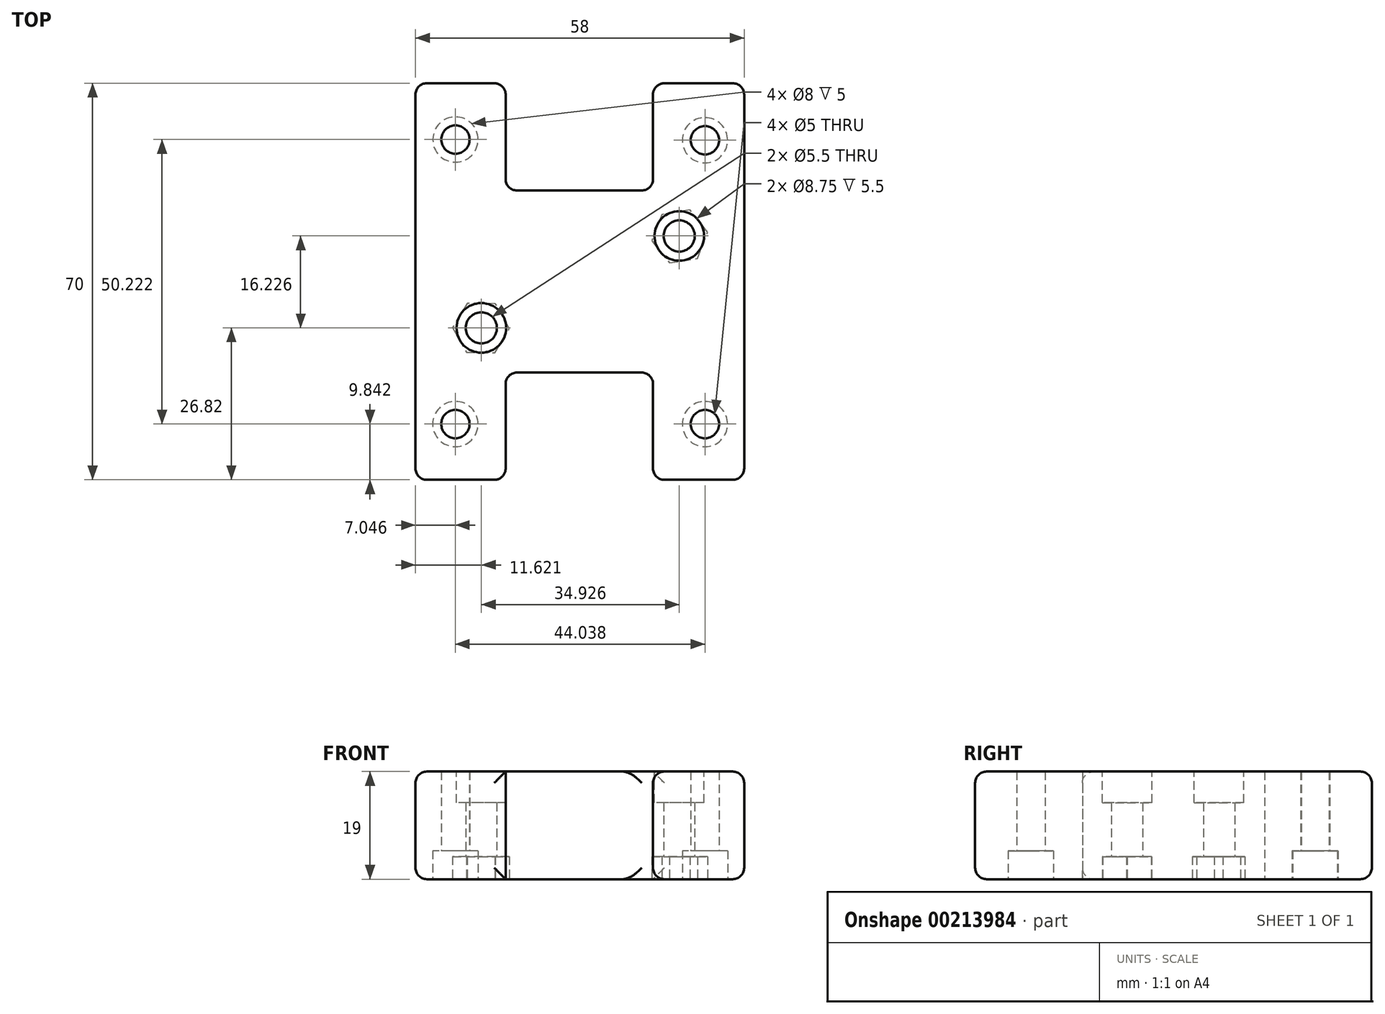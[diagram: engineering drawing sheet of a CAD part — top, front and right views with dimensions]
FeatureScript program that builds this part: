
annotation { "Feature Type Name" : "Feature", "Feature Type Description" : "" }
export const myFeature = defineFeature(function(context is Context, id is Id, definition is map)
    precondition{}
    {
        {
            var Q0;
            Q0=qCreatedBy(makeId("Top.planeOp"),FACE);
            var sketch = newSketch(context, id + "F0", { "sketchPlane" : qUnion([Q0])});
            skLineSegment(sketch, "E0.bottom", {"start": v(-29, 35) * mm, "end": v(29, 35) * mm});
            skLineSegment(sketch, "E0.top", {"start": v(-29, -35) * mm, "end": v(29, -35) * mm});
            skLineSegment(sketch, "E0.left", {"start": v(-29, 35) * mm, "end": v(-29, -35) * mm});
            skLineSegment(sketch, "E0.right", {"start": v(29, 35) * mm, "end": v(29, -35) * mm});
            skPoint(sketch, "E0.middle", {"position": v(0, 0) * mm});
            skSolve(sketch);
        }
        {
            var Q0;
            Q0=qCreatedBy(makeId("Top.planeOp"),FACE);
            var sketch = newSketch(context, id + "F1", { "sketchPlane" : qUnion([Q0])});
            skLineSegment(sketch, "E1", {"start": v(-28.94, -35.1) * mm, "end": v(-21.94, -35.1) * mm});
            skLineSegment(sketch, "E2", {"start": v(-28.94, -35.1) * mm, "end": v(-28.94, -25.1) * mm});
            skLineSegment(sketch, "E3", {"start": v(-28.94, -25.1) * mm, "end": v(29.13, -25.1) * mm});
            skLineSegment(sketch, "E4", {"start": v(-21.94, -35.1) * mm, "end": v(-21.94, 34.92) * mm});
            skLineSegment(sketch, "E5", {"start": v(29.13, -25.1) * mm, "end": v(29.13, -35.1) * mm});
            skLineSegment(sketch, "E6", {"start": v(29.13, -35.1) * mm, "end": v(22.13, -35.1) * mm});
            skLineSegment(sketch, "E7", {"start": v(22.13, -35.1) * mm, "end": v(22.13, 34.86) * mm});
            skLineSegment(sketch, "E8", {"start": v(22.13, 34.86) * mm, "end": v(29.13, 34.86) * mm});
            skLineSegment(sketch, "E9", {"start": v(29.13, 34.86) * mm, "end": v(29.13, 24.86) * mm});
            skLineSegment(sketch, "E10", {"start": v(29.13, 24.86) * mm, "end": v(-28.94, 24.86) * mm});
            skLineSegment(sketch, "E11", {"start": v(-28.94, 24.86) * mm, "end": v(-28.94, 34.86) * mm});
            skLineSegment(sketch, "E12", {"start": v(-28.94, 34.86) * mm, "end": v(-21.94, 34.92) * mm});
            skLineSegment(sketch, "E13", {"start": v(29.13, 34.86) * mm, "end": v(29.13, 7.96) * mm});
            skLineSegment(sketch, "E14", {"start": v(29.13, 7.96) * mm, "end": v(17.63, 7.96) * mm});
            skLineSegment(sketch, "E15", {"start": v(-28.94, -35.1) * mm, "end": v(-28.94, -8.2) * mm});
            skLineSegment(sketch, "E16", {"start": v(-28.94, -8.2) * mm, "end": v(-17.44, -8.2) * mm});
            skLineSegment(sketch, "E17", {"start": v(-28.94, -25.1) * mm, "end": v(-12.94, -25.1) * mm});
            skLineSegment(sketch, "E18", {"start": v(-12.94, -25.1) * mm, "end": v(-12.94, -16.1) * mm});
            skLineSegment(sketch, "E19", {"start": v(-12.94, -16.1) * mm, "end": v(-12.94, -35.1) * mm});
            skLineSegment(sketch, "E20.MirrorCS", {"start": v(12.94, -16.1) * mm, "end": v(12.94, -35.1) * mm});
            skLineSegment(sketch, "E21.MirrorCS", {"start": v(-12.94, 16.1) * mm, "end": v(-12.94, 35.1) * mm});
            skLineSegment(sketch, "E22.MirrorCS", {"start": v(12.94, 16.1) * mm, "end": v(12.94, 35.1) * mm});
            skSolve(sketch);
        }
        {
            var Q0;
            Q0=qCreatedBy(makeId("Top.planeOp"),FACE);
            var sketch = newSketch(context, id + "F2", { "sketchPlane" : qUnion([Q0])});
            skCircle(sketch, "E23", {"center": v(-21.94, 25.06) * mm, "radius": 4 * mm});
            skCircle(sketch, "E24", {"center": v(-21.95, -25.16) * mm, "radius": 4 * mm});
            skCircle(sketch, "E25", {"center": v(22.08, -25.16) * mm, "radius": 4 * mm});
            skCircle(sketch, "E26", {"center": v(22.08, 24.94) * mm, "radius": 4 * mm});
            skSolve(sketch);
        }
        {
            var Q0;
            Q0=qCreatedBy(makeId("Top.planeOp"),FACE);
            var sketch = newSketch(context, id + "F3", { "sketchPlane" : qUnion([Q0])});
            skCircle(sketch, "E27", {"center": v(-21.94, 25.06) * mm, "radius": 2.5 * mm});
            skCircle(sketch, "E28", {"center": v(22.08, 24.94) * mm, "radius": 2.5 * mm});
            skCircle(sketch, "E29", {"center": v(-21.95, -25.16) * mm, "radius": 2.5 * mm});
            skCircle(sketch, "E30", {"center": v(22.08, -25.16) * mm, "radius": 2.5 * mm});
            skSolve(sketch);
        }
        {
            var Q0;
            Q0=makeQuery(id+"F0.imprint","IMPRINT",FACE,{"disambiguationData":[TD([[makeQuery(id+"F0.imprint","IMPRINT",EDGE,{"derivedFrom":sQuery(id+"F0.wireOp",EDGE,"E0.bottom")}),-1.0]])]});
            extrude(context, id + "F4", {"entities" : qUnion([Q0]), "offsetDistance" : 25 * mm, "depth" : 19 * mm});
        }
        {
            var Q0;
            Q0=makeQuery(id+"F3.imprint","IMPRINT",FACE,{"disambiguationData":[TD([[makeQuery(id+"F3.imprint","IMPRINT",EDGE,{"derivedFrom":sQuery(id+"F3.wireOp",EDGE,"E27")}),1.0]])]});
            extrude(context, id + "F5", {"entities" : qUnion([Q0]), "operationType" : NewBodyOperationType.REMOVE, "depth" : 14 * mm});
        }
        {
            var Q0;
            Q0=makeQuery(id+"F2.imprint","IMPRINT",FACE,{"disambiguationData":[TD([[makeQuery(id+"F2.imprint","IMPRINT",EDGE,{"derivedFrom":sQuery(id+"F2.wireOp",EDGE,"E23")}),1.0]])]});
            extrude(context, id + "F6", {"entities" : qUnion([Q0]), "operationType" : NewBodyOperationType.REMOVE, "offsetDistance" : 25 * mm, "depth" : 5 * mm});
        }
        {
            var Q0;
            Q0 = qSketchRegion(id + "F3", true);
            extrude(context, id + "F7", {"entities" : qUnion([Q0]), "operationType" : NewBodyOperationType.REMOVE, "offsetDistance" : 25 * mm, "depth" : 19 * mm});
        }
        {
            var Q0;
            Q0 = qSketchRegion(id + "F2", true);
            extrude(context, id + "F8", {"entities" : qUnion([Q0]), "operationType" : NewBodyOperationType.REMOVE, "depth" : 5 * mm});
        }
        {
            var Q0;
            Q0=qCreatedBy(makeId("Top.planeOp"),FACE);
            var sketch = newSketch(context, id + "F9", { "sketchPlane" : qUnion([Q0])});
            skCircle(sketch, "E31", {"center": v(17.55, 8.05) * mm, "radius": 2.75 * mm});
            skCircle(sketch, "E32", {"center": v(-17.38, -8.18) * mm, "radius": 2.75 * mm});
            skSolve(sketch);
        }
        {
            var Q0;
            Q0 = qSketchRegion(id + "F9", true);
            extrude(context, id + "F10", {"entities" : qUnion([Q0]), "operationType" : NewBodyOperationType.REMOVE, "offsetDistance" : 25 * mm, "depth" : 19 * mm});
        }
        {
            var Q0;
            Q0=makeQuery(id+"F4.opExtrude","CAP_FACE",FACE,{"disambiguationData":[OSD([sQuery(id+"F0.wireOp",EDGE,"E0.bottom"),sQuery(id+"F0.wireOp",EDGE,"E0.top"),sQuery(id+"F0.wireOp",EDGE,"E0.left"),sQuery(id+"F0.wireOp",EDGE,"E0.right")])],"isStart":true});
            var sketch = newSketch(context, id + "F11", { "sketchPlane" : qUnion([Q0])});
            skCircle(sketch, "E33.cCircle", {"center": v(-17.44, 8.2) * mm, "radius": 5 * mm, "construction": true});
            skLineSegment(sketch, "E33.0", {"start": v(-20, 12.5) * mm, "end": v(-15, 12.57) * mm});
            skLineSegment(sketch, "E33.1", {"start": v(-15, 12.57) * mm, "end": v(-12.44, 8.28) * mm});
            skLineSegment(sketch, "E33.2", {"start": v(-12.44, 8.28) * mm, "end": v(-14.88, 3.91) * mm});
            skLineSegment(sketch, "E33.3", {"start": v(-14.88, 3.91) * mm, "end": v(-19.88, 3.84) * mm});
            skLineSegment(sketch, "E33.4", {"start": v(-19.88, 3.84) * mm, "end": v(-22.44, 8.14) * mm});
            skLineSegment(sketch, "E33.5", {"start": v(-22.44, 8.14) * mm, "end": v(-20, 12.5) * mm});
            skCircle(sketch, "E34.cCircle", {"center": v(17.63, -7.96) * mm, "radius": 5 * mm, "construction": true});
            skLineSegment(sketch, "E34.0", {"start": v(22.57, -8.74) * mm, "end": v(19.42, -12.63) * mm});
            skLineSegment(sketch, "E34.1", {"start": v(19.42, -12.63) * mm, "end": v(14.49, -11.85) * mm});
            skLineSegment(sketch, "E34.2", {"start": v(14.49, -11.85) * mm, "end": v(12.69, -7.19) * mm});
            skLineSegment(sketch, "E34.3", {"start": v(12.69, -7.19) * mm, "end": v(15.83, -3.3) * mm});
            skLineSegment(sketch, "E34.4", {"start": v(15.83, -3.3) * mm, "end": v(20.77, -4.07) * mm});
            skLineSegment(sketch, "E34.5", {"start": v(20.77, -4.07) * mm, "end": v(22.57, -8.74) * mm});
            skSolve(sketch);
        }
        {
            var Q0;
            Q0 = qSketchRegion(id + "F11", true);
            extrude(context, id + "F12", {"entities" : qUnion([Q0]), "operationType" : NewBodyOperationType.REMOVE, "oppositeDirection" : true, "offsetDistance" : 25 * mm, "depth" : 4 * mm});
        }
        {
            var Q0;
            Q0=qCreatedBy(makeId("Top.planeOp"),FACE);
            var sketch = newSketch(context, id + "F13", { "sketchPlane" : qUnion([Q0])});
            skLineSegment(sketch, "E35.bottom", {"start": v(-13.1, 16.07) * mm, "end": v(12.9, 16.07) * mm});
            skLineSegment(sketch, "E35.top", {"start": v(-13.1, 35.07) * mm, "end": v(12.9, 35.07) * mm});
            skLineSegment(sketch, "E35.left", {"start": v(-13.1, 16.07) * mm, "end": v(-13.1, 35.07) * mm});
            skLineSegment(sketch, "E35.right", {"start": v(12.9, 16.07) * mm, "end": v(12.9, 35.07) * mm});
            skLineSegment(sketch, "E36.MirrorCS", {"start": v(-13.1, -16.07) * mm, "end": v(12.9, -16.07) * mm});
            skLineSegment(sketch, "E37.MirrorCS", {"start": v(-13.1, -16.07) * mm, "end": v(-13.1, -35.07) * mm});
            skLineSegment(sketch, "E38.MirrorCS", {"start": v(12.9, -16.07) * mm, "end": v(12.9, -35.07) * mm});
            skLineSegment(sketch, "E39.MirrorCS", {"start": v(-13.1, -35.07) * mm, "end": v(12.9, -35.07) * mm});
            skSolve(sketch);
        }
        {
            var Q0;
            Q0 = qSketchRegion(id + "F13", true);
            extrude(context, id + "F14", {"entities" : qUnion([Q0]), "operationType" : NewBodyOperationType.REMOVE, "offsetDistance" : 25 * mm, "depth" : 19 * mm});
        }
        {
            var Q0;
            Q0=makeQuery(id+"F14.boolean.opBoolean","COPY",EDGE,{"derivedFrom":makeQuery(id+"F14.opExtrude","CAP_EDGE",EDGE,{"disambiguationData":[OSD([sQuery(id+"F13.wireOp",EDGE,"E35.left")])],"isStart":true})});
            var Q1;
            Q1=makeQuery(id+"F14.boolean.opBoolean","COPY",EDGE,{"derivedFrom":makeQuery(id+"F14.opExtrude","CAP_EDGE",EDGE,{"disambiguationData":[OSD([sQuery(id+"F13.wireOp",EDGE,"E35.bottom")])],"isStart":true})});
            var Q2;
            Q2=makeQuery(id+"F14.boolean.opBoolean","COPY",EDGE,{"derivedFrom":makeQuery(id+"F14.opExtrude","CAP_EDGE",EDGE,{"disambiguationData":[OSD([sQuery(id+"F13.wireOp",EDGE,"E35.right")])],"isStart":true})});
            var Q3;
            {var subQ0=sQuery(id+"F0.wireOp",EDGE,"E0.bottom");var subQ1=sQuery(id+"F0.wireOp",EDGE,"E0.left");Q3=makeQuery(id+"F14.boolean.opBoolean","SPLIT",EDGE,{"disambiguationData":[TD([makeQuery(id+"F4.opExtrude","SWEPT_FACE",FACE,{"disambiguationData":[OSD([subQ1])]})])],"derivedFrom":makeQuery(id+"F4.opExtrude","CAP_EDGE",EDGE,{"disambiguationData":[OSD([subQ0])],"isStart":true})});}
            var Q4;
            Q4=makeQuery(id+"F4.opExtrude","CAP_EDGE",EDGE,{"disambiguationData":[OSD([sQuery(id+"F0.wireOp",EDGE,"E0.left")])],"isStart":true});
            var Q5;
            {var subQ0=sQuery(id+"F0.wireOp",EDGE,"E0.left");var subQ1=sQuery(id+"F0.wireOp",EDGE,"E0.top");Q5=makeQuery(id+"F14.boolean.opBoolean","SPLIT",EDGE,{"disambiguationData":[TD([makeQuery(id+"F4.opExtrude","SWEPT_FACE",FACE,{"disambiguationData":[OSD([subQ0])]})])],"derivedFrom":makeQuery(id+"F4.opExtrude","CAP_EDGE",EDGE,{"disambiguationData":[OSD([subQ1])],"isStart":true})});}
            var Q6;
            Q6=makeQuery(id+"F14.boolean.opBoolean","COPY",EDGE,{"derivedFrom":makeQuery(id+"F14.opExtrude","CAP_EDGE",EDGE,{"disambiguationData":[OSD([sQuery(id+"F13.wireOp",EDGE,"E37.MirrorCS")])],"isStart":true})});
            var Q7;
            Q7=makeQuery(id+"F14.boolean.opBoolean","COPY",EDGE,{"derivedFrom":makeQuery(id+"F14.opExtrude","CAP_EDGE",EDGE,{"disambiguationData":[OSD([sQuery(id+"F13.wireOp",EDGE,"E36.MirrorCS")])],"isStart":true})});
            var Q8;
            Q8=makeQuery(id+"F14.boolean.opBoolean","COPY",EDGE,{"derivedFrom":makeQuery(id+"F14.opExtrude","CAP_EDGE",EDGE,{"disambiguationData":[OSD([sQuery(id+"F13.wireOp",EDGE,"E38.MirrorCS")])],"isStart":true})});
            var Q9;
            {var subQ0=sQuery(id+"F0.wireOp",EDGE,"E0.right");var subQ1=sQuery(id+"F0.wireOp",EDGE,"E0.top");Q9=makeQuery(id+"F14.boolean.opBoolean","SPLIT",EDGE,{"disambiguationData":[TD([makeQuery(id+"F4.opExtrude","SWEPT_FACE",FACE,{"disambiguationData":[OSD([subQ0])]})])],"derivedFrom":makeQuery(id+"F4.opExtrude","CAP_EDGE",EDGE,{"disambiguationData":[OSD([subQ1])],"isStart":true})});}
            var Q10;
            Q10=makeQuery(id+"F4.opExtrude","CAP_EDGE",EDGE,{"disambiguationData":[OSD([sQuery(id+"F0.wireOp",EDGE,"E0.right")])],"isStart":true});
            var Q11;
            {var subQ0=sQuery(id+"F0.wireOp",EDGE,"E0.bottom");var subQ1=sQuery(id+"F0.wireOp",EDGE,"E0.right");Q11=makeQuery(id+"F14.boolean.opBoolean","SPLIT",EDGE,{"disambiguationData":[TD([makeQuery(id+"F4.opExtrude","SWEPT_FACE",FACE,{"disambiguationData":[OSD([subQ1])]})])],"derivedFrom":makeQuery(id+"F4.opExtrude","CAP_EDGE",EDGE,{"disambiguationData":[OSD([subQ0])],"isStart":true})});}
            var Q12;
            Q12=makeQuery(id+"F14.boolean.opBoolean","INTERSECT",EDGE,{"derivedFrom":[makeQuery(id+"F4.opExtrude","SWEPT_FACE",FACE,{"disambiguationData":[OSD([sQuery(id+"F0.wireOp",EDGE,"E0.bottom")])]}),makeQuery(id+"F14.opExtrude","SWEPT_FACE",FACE,{"disambiguationData":[OSD([sQuery(id+"F13.wireOp",EDGE,"E35.left")])]})]});
            var Q13;
            Q13=makeQuery(id+"F14.boolean.opBoolean","COPY",EDGE,{"derivedFrom":makeQuery(id+"F14.opExtrude","SWEPT_EDGE",EDGE,{"disambiguationData":[OSD([sQuery(id+"F13.wireOp",EDGE,"E35.bottom"),sQuery(id+"F13.wireOp",EDGE,"E35.left")])]})});
            var Q14;
            Q14=makeQuery(id+"F14.boolean.opBoolean","INTERSECT",EDGE,{"derivedFrom":[makeQuery(id+"F4.opExtrude","SWEPT_FACE",FACE,{"disambiguationData":[OSD([sQuery(id+"F0.wireOp",EDGE,"E0.bottom")])]}),makeQuery(id+"F14.opExtrude","SWEPT_FACE",FACE,{"disambiguationData":[OSD([sQuery(id+"F13.wireOp",EDGE,"E35.right")])]})]});
            var Q15;
            Q15=makeQuery(id+"F4.opExtrude","SWEPT_EDGE",EDGE,{"disambiguationData":[OSD([sQuery(id+"F0.wireOp",EDGE,"E0.bottom"),sQuery(id+"F0.wireOp",EDGE,"E0.right")])]});
            var Q16;
            Q16=makeQuery(id+"F4.opExtrude","SWEPT_EDGE",EDGE,{"disambiguationData":[OSD([sQuery(id+"F0.wireOp",EDGE,"E0.bottom"),sQuery(id+"F0.wireOp",EDGE,"E0.left")])]});
            var Q17;
            {var subQ0=sQuery(id+"F0.wireOp",EDGE,"E0.bottom");var subQ1=sQuery(id+"F0.wireOp",EDGE,"E0.left");Q17=makeQuery(id+"F14.boolean.opBoolean","SPLIT",EDGE,{"disambiguationData":[TD([makeQuery(id+"F4.opExtrude","SWEPT_FACE",FACE,{"disambiguationData":[OSD([subQ1])]})])],"derivedFrom":makeQuery(id+"F4.opExtrude","CAP_EDGE",EDGE,{"disambiguationData":[OSD([subQ0])],"isStart":false})});}
            var Q18;
            Q18=makeQuery(id+"F14.boolean.opBoolean","COPY",EDGE,{"derivedFrom":makeQuery(id+"F14.opExtrude","CAP_EDGE",EDGE,{"disambiguationData":[OSD([sQuery(id+"F13.wireOp",EDGE,"E35.left")])],"isStart":false})});
            var Q19;
            Q19=makeQuery(id+"F14.boolean.opBoolean","COPY",EDGE,{"derivedFrom":makeQuery(id+"F14.opExtrude","CAP_EDGE",EDGE,{"disambiguationData":[OSD([sQuery(id+"F13.wireOp",EDGE,"E35.bottom")])],"isStart":false})});
            var Q20;
            {var subQ0=sQuery(id+"F0.wireOp",EDGE,"E0.bottom");var subQ1=sQuery(id+"F0.wireOp",EDGE,"E0.right");Q20=makeQuery(id+"F14.boolean.opBoolean","SPLIT",EDGE,{"disambiguationData":[TD([makeQuery(id+"F4.opExtrude","SWEPT_FACE",FACE,{"disambiguationData":[OSD([subQ1])]})])],"derivedFrom":makeQuery(id+"F4.opExtrude","CAP_EDGE",EDGE,{"disambiguationData":[OSD([subQ0])],"isStart":false})});}
            var Q21;
            Q21=makeQuery(id+"F4.opExtrude","CAP_EDGE",EDGE,{"disambiguationData":[OSD([sQuery(id+"F0.wireOp",EDGE,"E0.right")])],"isStart":false});
            var Q22;
            Q22=makeQuery(id+"F4.opExtrude","SWEPT_EDGE",EDGE,{"disambiguationData":[OSD([sQuery(id+"F0.wireOp",EDGE,"E0.top"),sQuery(id+"F0.wireOp",EDGE,"E0.right")])]});
            var Q23;
            Q23=makeQuery(id+"F14.boolean.opBoolean","COPY",EDGE,{"derivedFrom":makeQuery(id+"F14.opExtrude","CAP_EDGE",EDGE,{"disambiguationData":[OSD([sQuery(id+"F13.wireOp",EDGE,"E35.right")])],"isStart":false})});
            var Q24;
            Q24=makeQuery(id+"F4.opExtrude","SWEPT_EDGE",EDGE,{"disambiguationData":[OSD([sQuery(id+"F0.wireOp",EDGE,"E0.top"),sQuery(id+"F0.wireOp",EDGE,"E0.left")])]});
            var Q25;
            Q25=makeQuery(id+"F4.opExtrude","CAP_EDGE",EDGE,{"disambiguationData":[OSD([sQuery(id+"F0.wireOp",EDGE,"E0.left")])],"isStart":false});
            var Q26;
            Q26=makeQuery(id+"F14.boolean.opBoolean","INTERSECT",EDGE,{"derivedFrom":[makeQuery(id+"F4.opExtrude","SWEPT_FACE",FACE,{"disambiguationData":[OSD([sQuery(id+"F0.wireOp",EDGE,"E0.top")])]}),makeQuery(id+"F14.opExtrude","SWEPT_FACE",FACE,{"disambiguationData":[OSD([sQuery(id+"F13.wireOp",EDGE,"E37.MirrorCS")])]})]});
            var Q27;
            Q27=makeQuery(id+"F14.boolean.opBoolean","INTERSECT",EDGE,{"derivedFrom":[makeQuery(id+"F4.opExtrude","SWEPT_FACE",FACE,{"disambiguationData":[OSD([sQuery(id+"F0.wireOp",EDGE,"E0.top")])]}),makeQuery(id+"F14.opExtrude","SWEPT_FACE",FACE,{"disambiguationData":[OSD([sQuery(id+"F13.wireOp",EDGE,"E38.MirrorCS")])]})]});
            var Q28;
            Q28=makeQuery(id+"F14.boolean.opBoolean","COPY",EDGE,{"derivedFrom":makeQuery(id+"F14.opExtrude","CAP_EDGE",EDGE,{"disambiguationData":[OSD([sQuery(id+"F13.wireOp",EDGE,"E38.MirrorCS")])],"isStart":false})});
            var Q29;
            Q29=makeQuery(id+"F14.boolean.opBoolean","COPY",FACE,{"derivedFrom":makeQuery(id+"F14.opExtrude","SWEPT_FACE",FACE,{"disambiguationData":[OSD([sQuery(id+"F13.wireOp",EDGE,"E38.MirrorCS")])]})});
            var Q30;
            {var subQ0=sQuery(id+"F0.wireOp",EDGE,"E0.right");var subQ1=sQuery(id+"F0.wireOp",EDGE,"E0.top");Q30=makeQuery(id+"F14.boolean.opBoolean","SPLIT",EDGE,{"disambiguationData":[TD([makeQuery(id+"F4.opExtrude","SWEPT_FACE",FACE,{"disambiguationData":[OSD([subQ0])]})])],"derivedFrom":makeQuery(id+"F4.opExtrude","CAP_EDGE",EDGE,{"disambiguationData":[OSD([subQ1])],"isStart":false})});}
            var Q31;
            {var subQ0=sQuery(id+"F0.wireOp",EDGE,"E0.left");var subQ1=sQuery(id+"F0.wireOp",EDGE,"E0.top");Q31=makeQuery(id+"F14.boolean.opBoolean","SPLIT",EDGE,{"disambiguationData":[TD([makeQuery(id+"F4.opExtrude","SWEPT_FACE",FACE,{"disambiguationData":[OSD([subQ0])]})])],"derivedFrom":makeQuery(id+"F4.opExtrude","CAP_EDGE",EDGE,{"disambiguationData":[OSD([subQ1])],"isStart":false})});}
            var Q32;
            Q32=makeQuery(id+"F14.boolean.opBoolean","COPY",EDGE,{"derivedFrom":makeQuery(id+"F14.opExtrude","CAP_EDGE",EDGE,{"disambiguationData":[OSD([sQuery(id+"F13.wireOp",EDGE,"E36.MirrorCS")])],"isStart":false})});
            var Q33;
            Q33=makeQuery(id+"F14.boolean.opBoolean","COPY",EDGE,{"derivedFrom":makeQuery(id+"F14.opExtrude","CAP_EDGE",EDGE,{"disambiguationData":[OSD([sQuery(id+"F13.wireOp",EDGE,"E37.MirrorCS")])],"isStart":false})});
            var Q34;
            Q34=makeQuery(id+"F14.boolean.opBoolean","COPY",EDGE,{"derivedFrom":makeQuery(id+"F14.opExtrude","SWEPT_EDGE",EDGE,{"disambiguationData":[OSD([sQuery(id+"F13.wireOp",EDGE,"E36.MirrorCS"),sQuery(id+"F13.wireOp",EDGE,"E37.MirrorCS")])]})});
            var Q35;
            Q35=makeQuery(id+"F14.boolean.opBoolean","COPY",EDGE,{"derivedFrom":makeQuery(id+"F14.opExtrude","SWEPT_EDGE",EDGE,{"disambiguationData":[OSD([sQuery(id+"F13.wireOp",EDGE,"E35.bottom"),sQuery(id+"F13.wireOp",EDGE,"E35.right")])]})});
            fillet(context, id + "F15", {"entities" : qUnion([Q0, Q1, Q2, Q3, Q4, Q5, Q6, Q7, Q8, Q9, Q10, Q11, Q12, Q13, Q14, Q15, Q16, Q17, Q18, Q19, Q20, Q21, Q22, Q23, Q24, Q25, Q26, Q27, Q28, Q29, Q30, Q31, Q32, Q33, Q34, Q35]), "radius" : 2 * mm, "tangentPropagation" : true, "allowEdgeOverflow" : false});
        }
        {
            var Q0;
            Q0=makeQuery(id+"F4.opExtrude","CAP_FACE",FACE,{"disambiguationData":[OSD([sQuery(id+"F0.wireOp",EDGE,"E0.bottom"),sQuery(id+"F0.wireOp",EDGE,"E0.top"),sQuery(id+"F0.wireOp",EDGE,"E0.left"),sQuery(id+"F0.wireOp",EDGE,"E0.right")])],"isStart":false});
            var sketch = newSketch(context, id + "F16", { "sketchPlane" : qUnion([Q0])});
            skCircle(sketch, "E40", {"center": v(-17.38, -8.18) * mm, "radius": 4.38 * mm});
            skCircle(sketch, "E41", {"center": v(17.55, 8.05) * mm, "radius": 4.38 * mm});
            skSolve(sketch);
        }
        {
            var Q0;
            Q0=makeQuery(id+"F16.imprint","IMPRINT",FACE,{"disambiguationData":[TD([[makeQuery(id+"F16.imprint","IMPRINT",EDGE,{"derivedFrom":sQuery(id+"F16.wireOp",EDGE,"E40")}),1.0]])]});
            var Q1;
            Q1=makeQuery(id+"F16.imprint","IMPRINT",FACE,{"disambiguationData":[TD([[makeQuery(id+"F16.imprint","IMPRINT",EDGE,{"derivedFrom":sQuery(id+"F16.wireOp",EDGE,"E41")}),1.0]])]});
            extrude(context, id + "F17", {"entities" : qUnion([Q0, Q1]), "operationType" : NewBodyOperationType.REMOVE, "oppositeDirection" : true, "depth" : 5.5 * mm, "offsetDistance" : 25 * mm});
        }
    });
